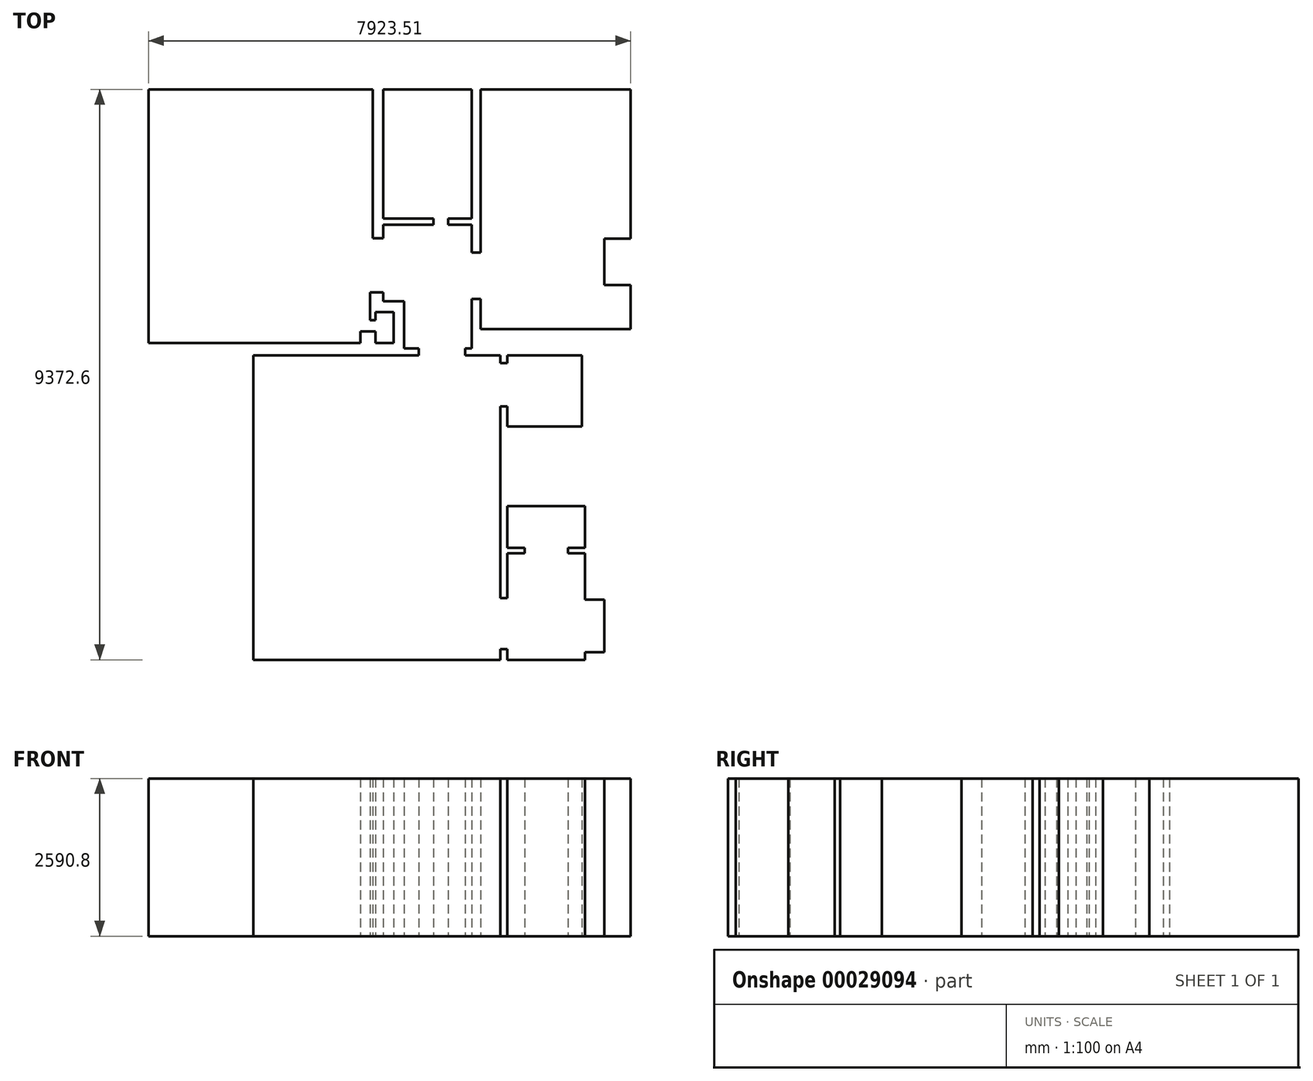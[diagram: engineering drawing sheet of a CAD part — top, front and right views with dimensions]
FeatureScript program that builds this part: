
annotation { "Feature Type Name" : "Feature", "Feature Type Description" : "" }
export const myFeature = defineFeature(function(context is Context, id is Id, definition is map)
    precondition{}
    {
        {
            var Q0;
            Q0=qCreatedBy(makeId("Top.planeOp"),FACE);
            var sketch = newSketch(context, id + "F0", { "sketchPlane" : qUnion([Q0])});
            skLineSegment(sketch, "E0", {"start": v(-317.44, 0) * mm, "end": v(-317.44, 121.92) * mm});
            skLineSegment(sketch, "E1", {"start": v(-317.44, 121.92) * mm, "end": v(0, 121.92) * mm});
            skLineSegment(sketch, "E2", {"start": v(0, 121.92) * mm, "end": v(0, 985.52) * mm});
            skLineSegment(sketch, "E3", {"start": v(0, 985.52) * mm, "end": v(-317.44, 985.52) * mm});
            skLineSegment(sketch, "E4", {"start": v(-317.44, 0) * mm, "end": v(-1587.44, 0) * mm});
            skLineSegment(sketch, "E5", {"start": v(-1587.44, 0) * mm, "end": v(-1587.44, 172.72) * mm});
            skLineSegment(sketch, "E6", {"start": v(-1587.44, 172.72) * mm, "end": v(-1701.74, 172.72) * mm});
            skLineSegment(sketch, "E7", {"start": v(-1701.74, 172.72) * mm, "end": v(-1701.74, 0) * mm});
            skLineSegment(sketch, "E8", {"start": v(-1701.74, 0) * mm, "end": v(-5765.74, 0) * mm});
            skLineSegment(sketch, "E9", {"start": v(-5765.74, 0) * mm, "end": v(-5765.74, 5003.8) * mm});
            skLineSegment(sketch, "E10", {"start": v(-317.44, 985.52) * mm, "end": v(-317.44, 1747.52) * mm});
            skLineSegment(sketch, "E11", {"start": v(-317.44, 1747.52) * mm, "end": v(-596.84, 1747.52) * mm});
            skLineSegment(sketch, "E12", {"start": v(-596.84, 1747.52) * mm, "end": v(-596.84, 1836.42) * mm});
            skLineSegment(sketch, "E13", {"start": v(-596.84, 1836.42) * mm, "end": v(-317.44, 1836.42) * mm});
            skLineSegment(sketch, "E14", {"start": v(-317.44, 1836.42) * mm, "end": v(-317.44, 2522.22) * mm});
            skLineSegment(sketch, "E15", {"start": v(-317.44, 2522.22) * mm, "end": v(-1587.44, 2522.22) * mm});
            skLineSegment(sketch, "E16", {"start": v(-1587.44, 2522.22) * mm, "end": v(-1587.44, 1836.42) * mm});
            skLineSegment(sketch, "E17", {"start": v(-1587.44, 1836.42) * mm, "end": v(-1308.04, 1836.42) * mm});
            skLineSegment(sketch, "E18", {"start": v(-1308.04, 1836.42) * mm, "end": v(-1308.04, 1747.52) * mm});
            skLineSegment(sketch, "E19", {"start": v(-1308.04, 1747.52) * mm, "end": v(-1587.44, 1747.52) * mm});
            skLineSegment(sketch, "E20", {"start": v(-1587.44, 1010.92) * mm, "end": v(-1701.74, 1010.92) * mm});
            skLineSegment(sketch, "E21", {"start": v(-1587.44, 1747.52) * mm, "end": v(-1587.44, 1010.92) * mm});
            skLineSegment(sketch, "E22", {"start": v(-1701.74, 1010.92) * mm, "end": v(-1701.74, 4165.6) * mm});
            skLineSegment(sketch, "E23", {"start": v(-1701.74, 4165.6) * mm, "end": v(-1587.44, 4165.6) * mm});
            skLineSegment(sketch, "E24", {"start": v(-1587.44, 4165.6) * mm, "end": v(-1587.44, 3835.4) * mm});
            skLineSegment(sketch, "E25", {"start": v(-1587.44, 3835.4) * mm, "end": v(-368.24, 3835.4) * mm});
            skLineSegment(sketch, "E26", {"start": v(-368.24, 3835.4) * mm, "end": v(-368.24, 5003.8) * mm});
            skLineSegment(sketch, "E27", {"start": v(-368.24, 5003.8) * mm, "end": v(-1587.44, 5003.8) * mm});
            skLineSegment(sketch, "E28", {"start": v(-1587.44, 5003.8) * mm, "end": v(-1587.44, 4876.8) * mm});
            skLineSegment(sketch, "E29", {"start": v(-1587.44, 4876.8) * mm, "end": v(-1701.74, 4876.8) * mm});
            skLineSegment(sketch, "E30", {"start": v(-1701.74, 4876.8) * mm, "end": v(-1701.74, 5003.8) * mm});
            skLineSegment(sketch, "E31", {"start": v(-1701.74, 5003.8) * mm, "end": v(-2285.94, 5003.8) * mm});
            skLineSegment(sketch, "E32", {"start": v(-2285.94, 5003.8) * mm, "end": v(-2285.94, 5118.1) * mm});
            skLineSegment(sketch, "E33", {"start": v(-3047.94, 5003.8) * mm, "end": v(-3047.94, 5118.1) * mm});
            skLineSegment(sketch, "E34", {"start": v(-5765.74, 5003.8) * mm, "end": v(-3047.94, 5003.8) * mm});
            skLineSegment(sketch, "E35", {"start": v(-3047.94, 5118.1) * mm, "end": v(-3284.59, 5118.1) * mm});
            skLineSegment(sketch, "E36", {"start": v(-3284.59, 5118.1) * mm, "end": v(-3284.59, 5889.93) * mm});
            skLineSegment(sketch, "E37", {"start": v(-3284.59, 5889.93) * mm, "end": v(-3628.63, 5889.93) * mm});
            skLineSegment(sketch, "E38", {"start": v(-3628.63, 5889.93) * mm, "end": v(-3628.63, 6038.36) * mm});
            skLineSegment(sketch, "E39", {"start": v(-2285.94, 5118.1) * mm, "end": v(-2173.79, 5118.1) * mm});
            skLineSegment(sketch, "E40", {"start": v(-2173.79, 5118.1) * mm, "end": v(-2173.79, 5930.9) * mm});
            skLineSegment(sketch, "E41", {"start": v(-2173.79, 5930.9) * mm, "end": v(-2026.56, 5930.9) * mm});
            skLineSegment(sketch, "E42", {"start": v(-2026.56, 5930.9) * mm, "end": v(-2026.56, 5435.6) * mm});
            skLineSegment(sketch, "E43", {"start": v(-2026.56, 5435.6) * mm, "end": v(437.24, 5435.6) * mm});
            skLineSegment(sketch, "E44", {"start": v(437.24, 5435.6) * mm, "end": v(437.24, 6159.5) * mm});
            skLineSegment(sketch, "E45", {"start": v(0, 6159.5) * mm, "end": v(437.24, 6159.5) * mm});
            skLineSegment(sketch, "E46", {"start": v(0, 6159.5) * mm, "end": v(0, 6921.5) * mm});
            skLineSegment(sketch, "E47", {"start": v(437.24, 6921.5) * mm, "end": v(0, 6921.5) * mm});
            skLineSegment(sketch, "E48", {"start": v(437.24, 6921.5) * mm, "end": v(437.24, 9372.6) * mm});
            skLineSegment(sketch, "E49", {"start": v(437.24, 9372.6) * mm, "end": v(-2026.56, 9372.6) * mm});
            skLineSegment(sketch, "E50", {"start": v(-2026.56, 9372.6) * mm, "end": v(-2026.56, 6692.9) * mm});
            skLineSegment(sketch, "E51", {"start": v(-2026.56, 6692.9) * mm, "end": v(-2173.79, 6692.9) * mm});
            skLineSegment(sketch, "E52", {"start": v(-2173.79, 6692.9) * mm, "end": v(-2173.79, 7147.13) * mm});
            skLineSegment(sketch, "E53", {"start": v(-2173.79, 7147.13) * mm, "end": v(-2561.24, 7147.13) * mm});
            skLineSegment(sketch, "E54", {"start": v(-2561.24, 7147.13) * mm, "end": v(-2561.24, 7248.68) * mm});
            skLineSegment(sketch, "E55", {"start": v(-2561.24, 7248.68) * mm, "end": v(-2173.79, 7248.68) * mm});
            skLineSegment(sketch, "E56", {"start": v(-2173.79, 7248.68) * mm, "end": v(-2173.79, 9372.6) * mm});
            skLineSegment(sketch, "E57", {"start": v(-2173.79, 9372.6) * mm, "end": v(-3627.84, 9372.6) * mm});
            skLineSegment(sketch, "E58", {"start": v(-3627.84, 9372.6) * mm, "end": v(-3627.84, 7248.68) * mm});
            skLineSegment(sketch, "E59", {"start": v(-3627.84, 7248.68) * mm, "end": v(-2804.95, 7248.68) * mm});
            skLineSegment(sketch, "E60", {"start": v(-2804.95, 7248.68) * mm, "end": v(-2804.95, 7147.13) * mm});
            skLineSegment(sketch, "E61", {"start": v(-2804.95, 7147.13) * mm, "end": v(-3628.63, 7147.13) * mm});
            skLineSegment(sketch, "E62", {"start": v(-3628.63, 7147.13) * mm, "end": v(-3628.63, 6924.39) * mm});
            skLineSegment(sketch, "E63", {"start": v(-3628.63, 6924.39) * mm, "end": v(-3803.27, 6924.39) * mm});
            skLineSegment(sketch, "E64", {"start": v(-3803.27, 6924.39) * mm, "end": v(-3803.27, 9372.6) * mm});
            skLineSegment(sketch, "E65", {"start": v(-3803.27, 9372.6) * mm, "end": v(-7486.27, 9372.6) * mm});
            skLineSegment(sketch, "E66", {"start": v(-7486.27, 9372.6) * mm, "end": v(-7486.27, 5207) * mm});
            skLineSegment(sketch, "E67", {"start": v(-7486.27, 5207) * mm, "end": v(-4006.55, 5207) * mm});
            skLineSegment(sketch, "E68", {"start": v(-4006.55, 5207) * mm, "end": v(-4006.55, 5394.6) * mm});
            skLineSegment(sketch, "E69", {"start": v(-4006.55, 5394.6) * mm, "end": v(-3754.23, 5394.6) * mm});
            skLineSegment(sketch, "E70", {"start": v(-3754.23, 5394.6) * mm, "end": v(-3754.23, 5207) * mm});
            skLineSegment(sketch, "E71", {"start": v(-3754.23, 5207) * mm, "end": v(-3456.74, 5207) * mm});
            skLineSegment(sketch, "E72", {"start": v(-3456.74, 5207) * mm, "end": v(-3456.74, 5710.46) * mm});
            skLineSegment(sketch, "E73", {"start": v(-3456.74, 5710.46) * mm, "end": v(-3754.23, 5710.46) * mm});
            skLineSegment(sketch, "E74", {"start": v(-3754.23, 5710.46) * mm, "end": v(-3754.23, 5578.4) * mm});
            skLineSegment(sketch, "E75", {"start": v(-3754.23, 5578.4) * mm, "end": v(-3842.9, 5578.4) * mm});
            skLineSegment(sketch, "E76", {"start": v(-3842.9, 5578.4) * mm, "end": v(-3842.9, 6038.36) * mm});
            skLineSegment(sketch, "E77", {"start": v(-3842.9, 6038.36) * mm, "end": v(-3628.63, 6038.36) * mm});
            skSolve(sketch);
        }
        {
            var Q0;
            Q0 = qSketchRegion(id + "F0", true);
            extrude(context, id + "F1", {"entities" : qUnion([Q0]), "depth" : 2590.8 * mm});
        }
    });
